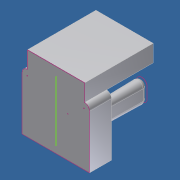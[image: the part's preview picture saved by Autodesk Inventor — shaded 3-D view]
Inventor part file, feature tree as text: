
AUTODESK INVENTOR PART (.ipt)
format: ipt  version: unknown  size: 267,776 bytes
history: native  units: in
note: dims shown in document units (in); Inventor stores cm internally (conversion verified against a paired STEP export)
features: other x20, sketch x6, extrude x4, fillet x1
ambient origin geometry x8: Origin, YZ Plane, XZ Plane, XY Plane, X Axis, Y Axis, Z Axis, Center Point
feature tree (31):
  sketch  "Sketch1"  dims[d15=0.1437in d18=0.69in d19=-0.0069in]
  extrude  "Extrusion2"  Depth=0.69in
  extrude  "Extrusion3"  Depth=0.25in
  extrude  "Extrusion4"  Depth=0.06in
  sketch  "Sketch4"
  fillet  "Fillet1"  Radius=0.076in
  extrude  "Extrusion5"  [1 undecoded]
  sketch  "Sketch7"
  sketch  "Sketch2"  dims[d25=0.25in d26=0.0in d27=0.25in]
  sketch  "Sketch3"  dims[d28=0.94in d29=0.0in d30=0.06in d31=0.076in d32=0.0in]
  sketch  "Sketch5"
  other  "Composite1"
  other  "Composite2"
  other  "Composite3"
  other  "Composite4"
  other  "Composite5"
  other  "Composite6"
  other  "Composite7"
  other  "Composite8"
  other  "Composite9"
  other  "Composite10"
  other  "Srf1"
  other  "Srf2"
  other  "Srf3"
  other  "Srf4"
  other  "Srf5"
  other  "Srf6"
  other  "Srf7"
  other  "Srf8"
  other  "Srf9"
  other  "Srf10"
note: 1 required parameter value undecoded (feature->parameter linkage not recoverable at this tier; creation-order binding heuristic only, values carry confidence <= 0.55)
